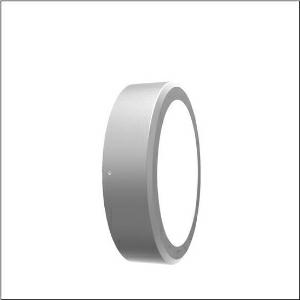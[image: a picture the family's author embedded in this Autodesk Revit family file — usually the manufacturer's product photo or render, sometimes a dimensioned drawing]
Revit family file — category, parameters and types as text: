
# Revit family: cl_31_bulkhead_5cl721603
name_source: partatom
category: Lighting Fixtures
units: mm (PartAtom-declared; Revit-internal decimal feet)

## family parameters
Cut with Voids When Loaded = No
Host = Face
Light Source = No
Part Type = Normal
Room Calculation Point = No
Round Connector Dimension = Use Diameter
Shared = No

## types (1)
- --- (1 x LED, 1570 lm, 14.9 W, 3000K)
    Apparent Load = 15 VA
    CIE Flux Codes = 46 78 95 100 100
    Color Rendering = 80
    Color Temperature = 3000K
    Default Elevation = 1800 mm
    Description = CL 31 Bulkhead, wall and ceiling luminaire, primary light control with reflector, primary optical cover: cover panel, of PC, opal, primary light characteristic: symmetric, installation type: surface-mounted, LED, rated luminous flux: 1.575lm, luminous efficacy: 105lm/W, light colour: 830, colour temperature: 3000K, control gear: DALI, with terminal, 5-pole, max. 2.5mm², mains connection: 220..240V, AC, 50/60Hz, rated input power: 15W, luminaire housing, round, of aluminium, powder-coated, SITECO metallic grey, diameter: 264mm, height: 63mm, protection rating (complete): IP65, insulation class (complete): insulation class I (protective earthing), certification: CE, ENEC, impact resistance: IK09, permissible operating ambient temperature for outdoor applications: -20..+50°C, packaging unit: 1 piece
    Height = 63 mm
    Lamp = 1 x LED
    Lamp Light Flux = 1570 lm
    Lamp Power = 14.9 W
    Lamp count = 1
    Length = 264 mm
    Luminous efficacy = 105 lm/W
    Manufacturer = Siteco
    ModVariant = No
    Model = 5CL721603
    Mounting Place = Wall
    Mounting Type = Surface mounted
    Number of Poles = 1
    OnlyDefault = Yes
    Power Factor = 1
    Product Name = CL 31 Bulkhead
    Product group = wall and ceiling luminaire | wall mounted
    ProductGroupID = 2001
    Protection Class = Protection class I
    Protection Degree = IP 65
    RLX_Detail_Level = 1
    RLX_Emergency_Light_Flux = 0 lm
    RLX_Emergency_Type = 0
    RLX_Emergency_Type_DB = No
    RlxData = <blob elided: 36861 chars, md5=f5ab3571>
    Socket = socket
    Standby Power = 0 W
    System Light Flux = 1570 lm
    System Power = 15 W
    Type Comments = factory setting: luminous flux: 100 % | dim-lin: 254 | 347 mA
    Type Image = l_1006885.jpg
    URL = http://relux.com
    VarID = @adj_192849
    Voltage = 0 V
    Weight = 0.00 kg
    Width = 0 mm  [stored 0 ft]

note: [stored X ft] marks values corroborated as IEEE doubles in the binary element streams (Revit-internal decimal feet)

## geometry (parser evidence)
native form markers: Blend x4, Sweep x9
no freeform markers — native parametric forms only
